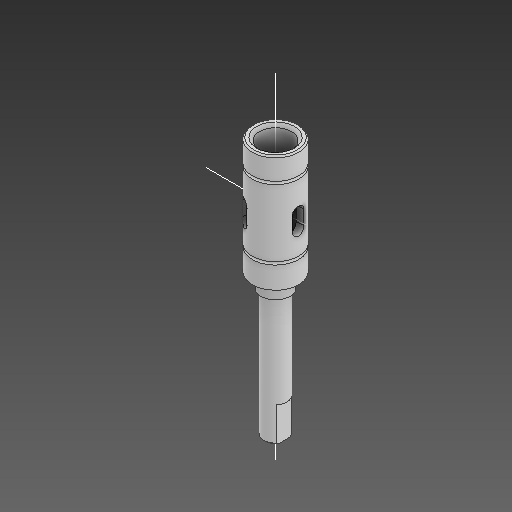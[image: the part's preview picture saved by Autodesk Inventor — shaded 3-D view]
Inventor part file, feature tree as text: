
AUTODESK INVENTOR PART (.ipt)
format: ipt  version: 2021 (Build 250183000, 183)  size: 287,232 bytes
history: native  units: mm
features: sketch x10, extrude x6, other x5, revolve x3, plane x3, chamfer x3, pattern_circular x1, hole x1
ambient origin geometry x8: Origin, YZ Plane, XZ Plane, XY Plane, X Axis, Y Axis, Z Axis, Center Point
bodies: Solid1 (feature_tree)
feature tree (32):
  revolve  "Revolution1"  [1 undecoded]
  plane  "Work Plane1"
  extrude  "Extrusion1"  TaperAngle=90.0deg  [1 undecoded]
  chamfer  "Chamfer1"  Distance=10.0mm
  pattern_circular  "Circular Pattern1"  Count=3 Angle=360.0deg
  plane  "Work Plane2"
  extrude  "Extrusion2"  Depth=0.1mm
  extrude  "Extrusion4"  Depth=10.0mm
  extrude  "Extrusion5"  Depth=2.5mm TaperAngle=0.0deg
  other  "Work Axis1"
  revolve  "Revolution2"  [1 undecoded]
  extrude  "Extrusion6"  Depth=10.0mm
  other  "Work Axis2"
  chamfer  "Chamfer4"  Angle=90.0deg  [1 undecoded]
  revolve  "Revolution3"  [1 undecoded]
  chamfer  "Chamfer5"  Distance=0.25mm Angle=45.0deg
  other  "Work Axis3"
  plane  "Work Plane3"
  hole  "Hole1"  [1 undecoded]
  extrude  "Extrusion8"  TaperAngle=90.0deg  [1 undecoded]
  sketch  "Sketch1"  dims[d0=8.0mm d2=20.0mm d5=5.5mm]
  sketch  "Sketch2"  dims[d6=16.0mm d7=90.0deg]
  sketch  "Sketch3"  dims[d8=10.5mm]
  other  "Srf1"
  sketch  "Sketch5"  dims[d9=2.0mm]
  sketch  "Sketch6"  dims[d10=2.5mm d11=10.0mm d12=0.0mm]
  sketch  "Sketch7"  dims[d13=0.5mm d14=2.0mm d15=45.0deg d16=30.0mm d17=360.0deg]
  sketch  "Sketch8"  dims[d19=90.0deg d20=0.1mm]
  sketch  "Sketch10"  dims[d21=10.0mm d22=0.0mm d24=1.0mm]
  sketch  "Sketch11"  dims[d28=5.0mm d29=2.5mm d30=0.0mm]
  sketch  "Sketch12"  dims[d33=4.0mm d34=22.0mm d35=0.0mm d42=0.25mm d43=90.0deg d44=10.0mm d45=0.0mm d53=0.25mm d54=2.0mm d55=45.0deg d57=0.5mm d59=90.0deg d60=0.25mm d61=2.0mm d62=45.0deg d63=8.0mm d66=0.5mm d70=4.4mm d71=3.0mm d72=5.5mm d73=6.0mm d74=4.0mm d75=2.0mm d76=90.0deg d77=18.0mm d78=20.594885mm d81=4.0mm d82=16.0mm d83=0.5mm d84=6.0mm d85=10.0mm d86=0.0mm]
  other  "Unwrap1"
note: 7 required parameter values undecoded (feature->parameter linkage not recoverable at this tier; creation-order binding heuristic only, values carry confidence <= 0.55)